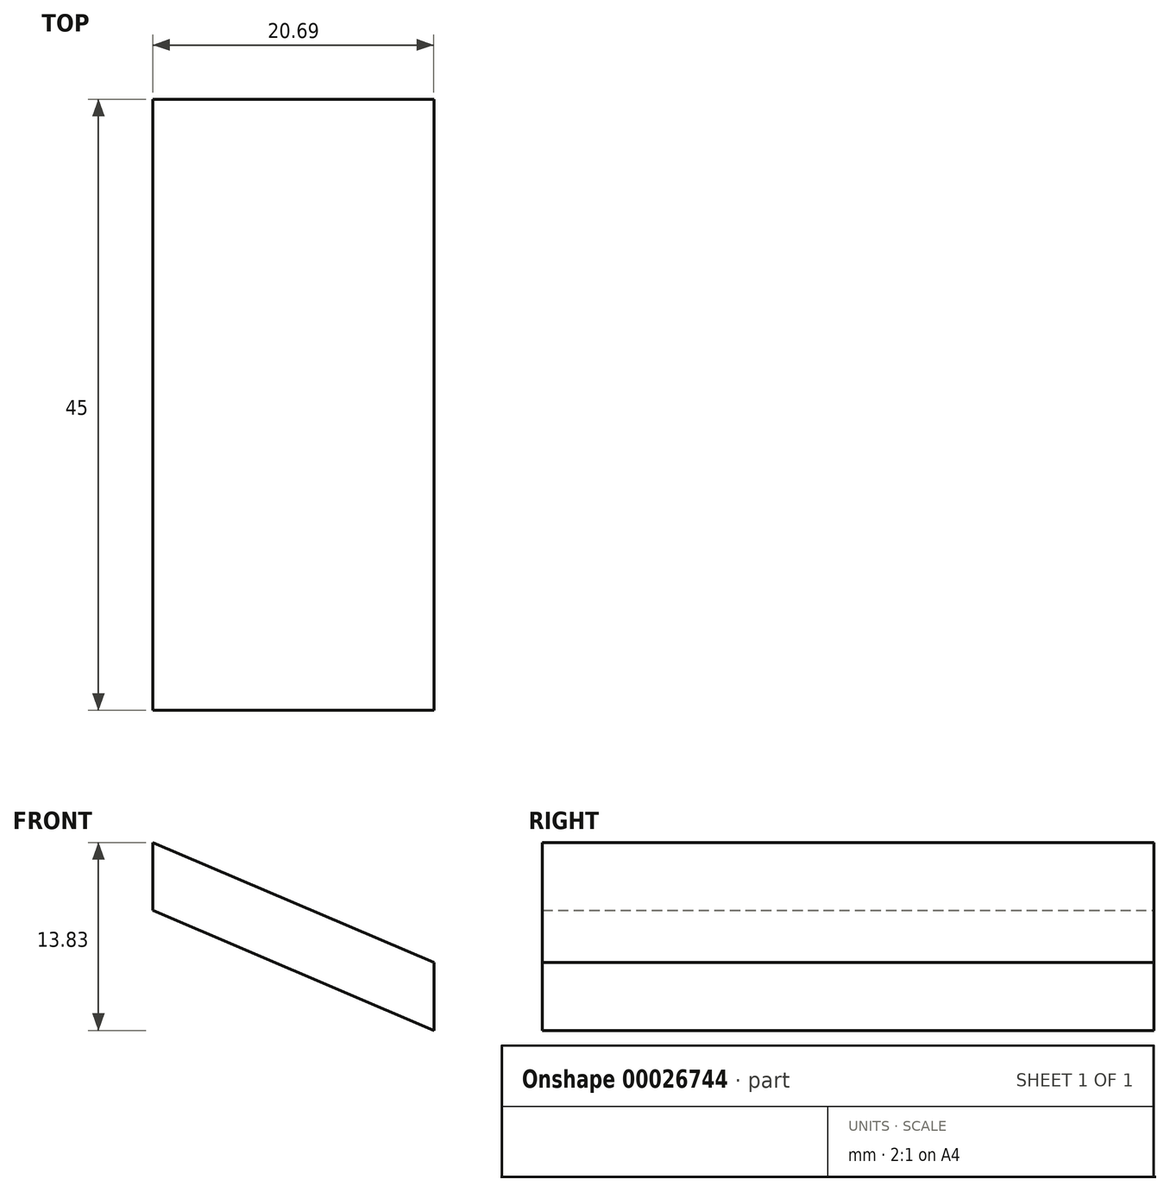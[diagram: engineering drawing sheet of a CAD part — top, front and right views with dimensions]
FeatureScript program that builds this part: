
annotation { "Feature Type Name" : "Feature", "Feature Type Description" : "" }
export const myFeature = defineFeature(function(context is Context, id is Id, definition is map)
    precondition{}
    {
        {
            var Q0;
            Q0=qCreatedBy(makeId("Front.planeOp"),FACE);
            var sketch = newSketch(context, id + "F0", { "sketchPlane" : qUnion([Q0])});
            skLineSegment(sketch, "E0", {"start": v(28.33, 5) * mm, "end": v(28.33, 0) * mm});
            skLineSegment(sketch, "E1", {"start": v(28.33, 0) * mm, "end": v(7.64, 8.83) * mm});
            skLineSegment(sketch, "E2", {"start": v(7.64, 8.83) * mm, "end": v(7.64, 13.83) * mm});
            skLineSegment(sketch, "E3", {"start": v(7.64, 13.83) * mm, "end": v(28.33, 5) * mm});
            skSolve(sketch);
        }
        {
            var Q0;
            Q0=makeQuery(id+"F0.imprint","IMPRINT",FACE,{"disambiguationData":[TD([[makeQuery(id+"F0.imprint","IMPRINT",EDGE,{"derivedFrom":sQuery(id+"F0.wireOp",EDGE,"E0")}),-1.0]])]});
            extrude(context, id + "F1", {"entities" : qUnion([Q0]), "depth" : 45 * mm});
        }
    });
